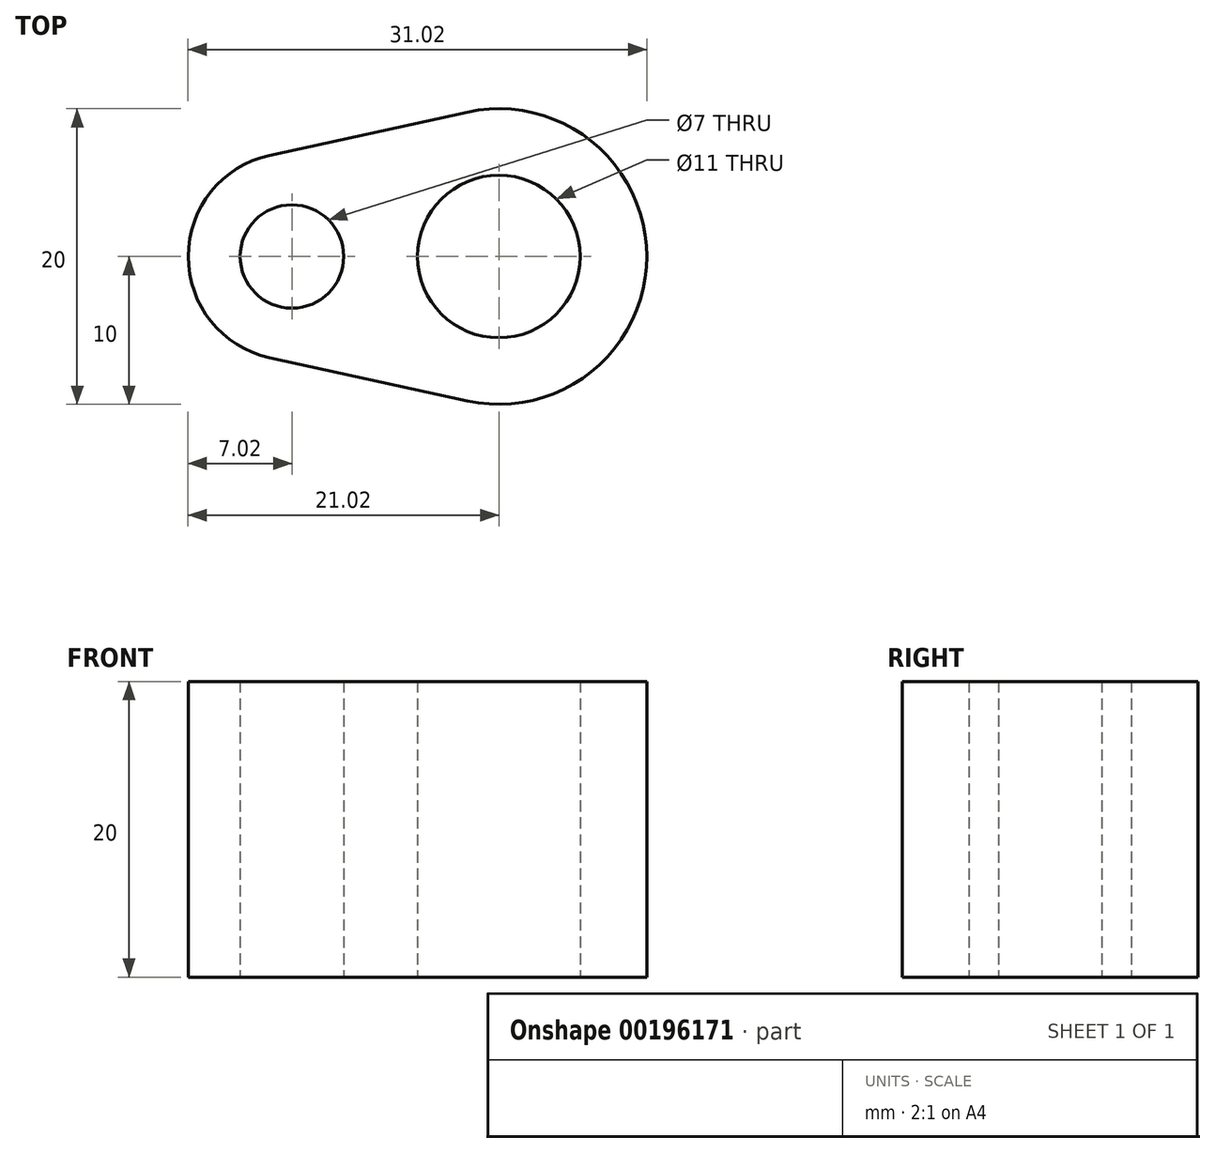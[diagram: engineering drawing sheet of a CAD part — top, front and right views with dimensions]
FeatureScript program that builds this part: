
annotation { "Feature Type Name" : "Feature", "Feature Type Description" : "" }
export const myFeature = defineFeature(function(context is Context, id is Id, definition is map)
    precondition{}
    {
        {
            var Q0;
            Q0=qCreatedBy(makeId("Top.planeOp"),FACE);
            cPlane(context, id + "F0", {"entities" : qUnion([Q0]), "cplaneType" : CPlaneType.OFFSET, "offset" : 20 * mm, "width" : 150 * mm, "height" : 150 * mm});
        }
        {
            var Q0;
            Q0=qCreatedBy(makeId("Top.planeOp"),FACE);
            var sketch = newSketch(context, id + "F1", { "sketchPlane" : qUnion([Q0])});
            skCircle(sketch, "E0", {"center": v(0, 0) * mm, "radius": 5.5 * mm});
            skSolve(sketch);
        }
        {
            var Q0;
            Q0=qCreatedBy(makeId("Top.planeOp"),FACE);
            var sketch = newSketch(context, id + "F2", { "sketchPlane" : qUnion([Q0])});
            skCircle(sketch, "E1", {"center": v(0, 0) * mm, "radius": 7 * mm});
            skSolve(sketch);
        }
        {
            var Q0;
            Q0=qCreatedBy(makeId("Top.planeOp"),FACE);
            var sketch = newSketch(context, id + "F3", { "sketchPlane" : qUnion([Q0])});
            skCircle(sketch, "E2", {"center": v(-14, 0) * mm, "radius": 3.5 * mm});
            skSolve(sketch);
        }
        {
            var Q0;
            Q0=qCreatedBy(makeId("Top.planeOp"),FACE);
            var sketch = newSketch(context, id + "F4", { "sketchPlane" : qUnion([Q0])});
            skArc(sketch, "E3", {"start": v(-2.14, -9.77) * mm, "mid": v(10, 0) * mm, "end": v(-2.14, 9.77) * mm});
            skArc(sketch, "E4", {"start": v(-15.51, 6.84) * mm, "mid": v(-21.02, 0) * mm, "end": v(-15.51, -6.84) * mm});
            skLineSegment(sketch, "E5", {"start": v(-2.14, 9.77) * mm, "end": v(-15.51, 6.84) * mm});
            skLineSegment(sketch, "E6", {"start": v(-2.14, -9.77) * mm, "end": v(-15.51, -6.84) * mm});
            skSolve(sketch);
        }
        {
            var Q0;
            Q0=makeQuery(id+"F4.imprint","IMPRINT",FACE,{"disambiguationData":[TD([[makeQuery(id+"F4.imprint","IMPRINT",EDGE,{"derivedFrom":sQuery(id+"F4.wireOp",EDGE,"E3")}),1.0]])]});
            extrude(context, id + "F5", {"entities" : qUnion([Q0]), "depth" : 20 * mm});
        }
        {
            var Q0;
            Q0 = qSketchRegion(id + "F3", true);
            var Q1;
            Q1=sQuery(id+"F3.wireOp",EDGE,"E2");
            extrude(context, id + "F6", {"entities" : qUnion([Q0]), "operationType" : NewBodyOperationType.REMOVE, "surfaceEntities" : qUnion([Q1]), "depth" : 20 * mm});
        }
        {
            var Q0;
            Q0 = qSketchRegion(id + "F1", true);
            extrude(context, id + "F7", {"entities" : qUnion([Q0]), "operationType" : NewBodyOperationType.REMOVE, "depth" : 20 * mm});
        }
    });
